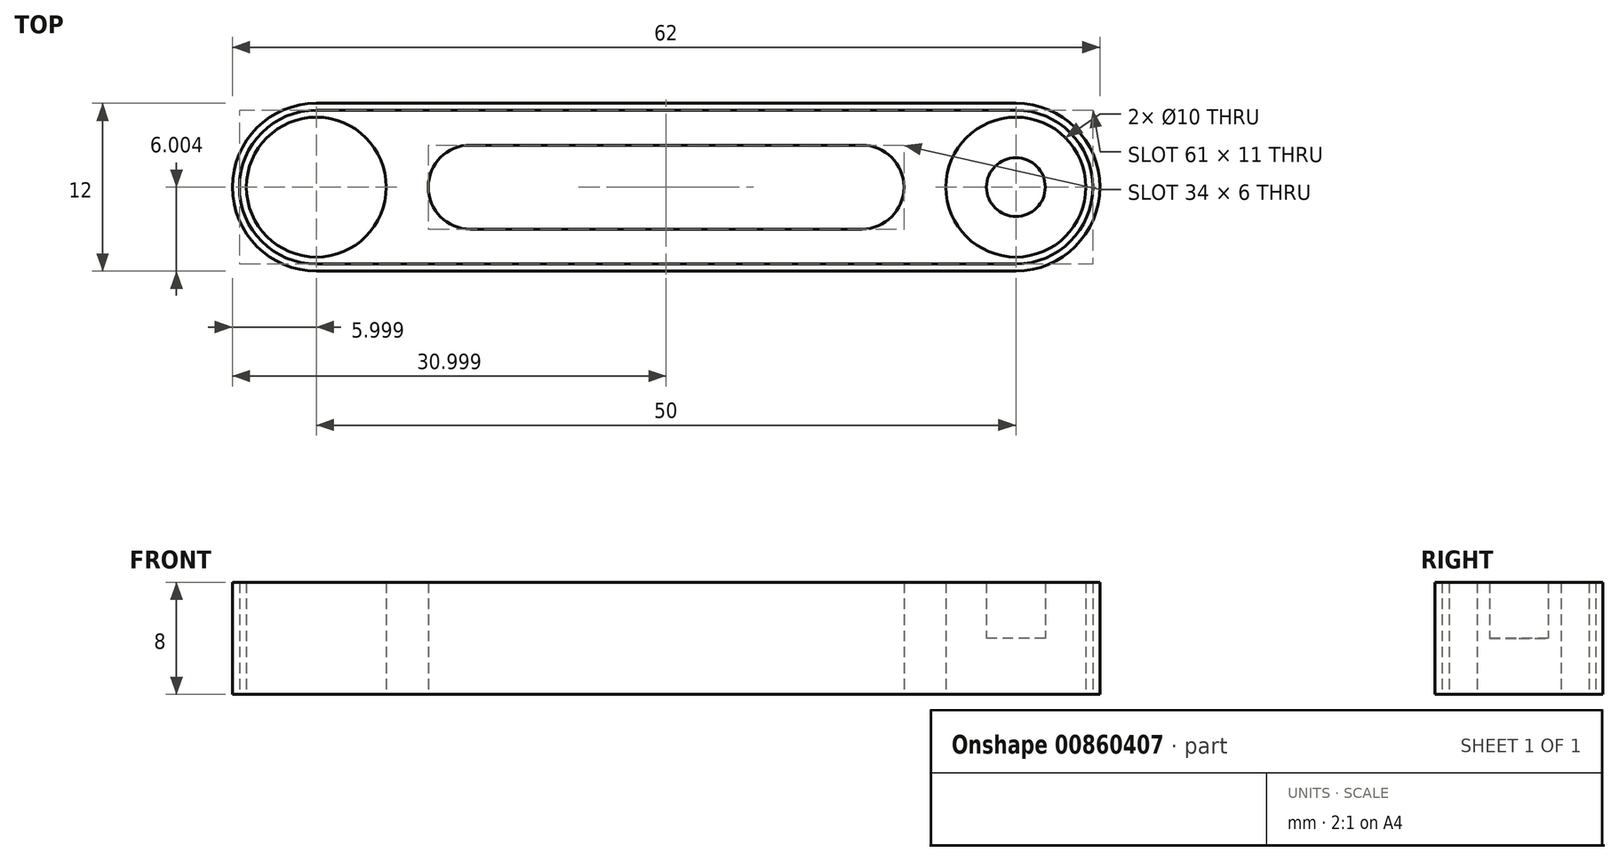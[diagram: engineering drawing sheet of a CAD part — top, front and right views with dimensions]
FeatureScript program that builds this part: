
annotation { "Feature Type Name" : "Feature", "Feature Type Description" : "" }
export const myFeature = defineFeature(function(context is Context, id is Id, definition is map)
    precondition{}
    {
        {
            var Q0;
            Q0=qCreatedBy(makeId("Top.planeOp"),FACE);
            var sketch = newSketch(context, id + "F0", { "sketchPlane" : qUnion([Q0])});
            skLineSegment(sketch, "E0", {"start": v(-96.16, -25.4) * mm, "end": v(-46.16, -25.4) * mm});
            skLineSegment(sketch, "E1", {"start": v(-46.16, -13.4) * mm, "end": v(-96.16, -13.4) * mm});
            skCircle(sketch, "E2", {"center": v(-96.16, -19.4) * mm, "radius": 2.1 * mm});
            skCircle(sketch, "E3", {"center": v(-46.16, -19.4) * mm, "radius": 2.1 * mm});
            skLineSegment(sketch, "E4", {"start": v(-9.27, -13.4) * mm, "end": v(-9.27, -25.4) * mm});
            skLineSegment(sketch, "E5", {"start": v(-1.27, -24.9) * mm, "end": v(-1.27, -13.9) * mm});
            skLineSegment(sketch, "E6", {"start": v(-1.77, -13.4) * mm, "end": v(-9.27, -13.4) * mm});
            skLineSegment(sketch, "E7", {"start": v(-9.27, -17.3) * mm, "end": v(-5.27, -17.3) * mm});
            skLineSegment(sketch, "E8", {"start": v(-9.27, -21.5) * mm, "end": v(-5.27, -21.5) * mm});
            skLineSegment(sketch, "E9", {"start": v(-5.27, -15.4) * mm, "end": v(-1.27, -15.4) * mm});
            skLineSegment(sketch, "E10", {"start": v(-5.27, -23.4) * mm, "end": v(-1.27, -23.4) * mm});
            skCircle(sketch, "E11", {"center": v(-96.16, -19.4) * mm, "radius": 4 * mm});
            skCircle(sketch, "E12", {"center": v(-46.16, -19.4) * mm, "radius": 4 * mm});
            skLineSegment(sketch, "E13", {"start": v(-5.27, -15.4) * mm, "end": v(-5.27, -23.4) * mm});
            skLineSegment(sketch, "E14", {"start": v(-85.16, -16.4) * mm, "end": v(-57.16, -16.4) * mm});
            skLineSegment(sketch, "E15", {"start": v(-57.16, -22.4) * mm, "end": v(-85.16, -22.4) * mm});
            skArc(sketch, "E16", {"start": v(-57.16, -22.4) * mm, "mid": v(-54.16, -19.4) * mm, "end": v(-57.16, -16.4) * mm});
            skArc(sketch, "E17", {"start": v(-85.16, -16.4) * mm, "mid": v(-88.16, -19.4) * mm, "end": v(-85.16, -22.4) * mm});
            skLineSegment(sketch, "E18", {"start": v(-9.27, -16.4) * mm, "end": v(-3.27, -16.4) * mm});
            skLineSegment(sketch, "E19", {"start": v(-3.27, -16.4) * mm, "end": v(-3.27, -22.4) * mm});
            skLineSegment(sketch, "E20", {"start": v(-9.27, -22.4) * mm, "end": v(-3.27, -22.4) * mm});
            skArc(sketch, "E21", {"start": v(-96.16, -13.4) * mm, "mid": v(-102.16, -19.4) * mm, "end": v(-96.16, -25.4) * mm});
            skArc(sketch, "E22", {"start": v(-46.16, -25.4) * mm, "mid": v(-40.16, -19.4) * mm, "end": v(-46.16, -13.4) * mm});
            skLineSegment(sketch, "E23", {"start": v(-46.16, -13.9) * mm, "end": v(-96.16, -13.9) * mm});
            skLineSegment(sketch, "E24", {"start": v(-96.16, -24.9) * mm, "end": v(-46.16, -24.9) * mm});
            skArc(sketch, "E25", {"start": v(-46.16, -24.9) * mm, "mid": v(-40.66, -19.4) * mm, "end": v(-46.16, -13.9) * mm});
            skArc(sketch, "E26", {"start": v(-96.16, -13.9) * mm, "mid": v(-101.66, -19.4) * mm, "end": v(-96.16, -24.9) * mm});
            skLineSegment(sketch, "E27", {"start": v(-9.27, -25.4) * mm, "end": v(-1.77, -25.4) * mm});
            skLineSegment(sketch, "E28", {"start": v(-1.77, -25.4) * mm, "end": v(-1.27, -24.9) * mm});
            skLineSegment(sketch, "E29", {"start": v(-1.77, -13.4) * mm, "end": v(-1.27, -13.9) * mm});
            skLineSegment(sketch, "E30", {"start": v(-1.77, -13.4) * mm, "end": v(-1.77, -25.4) * mm});
            skCircle(sketch, "E31", {"center": v(-46.16, -19.4) * mm, "radius": 5 * mm});
            skCircle(sketch, "E32", {"center": v(-96.16, -19.4) * mm, "radius": 5 * mm});
            skLineSegment(sketch, "E33", {"start": v(-8.27, -14.4) * mm, "end": v(-8.27, -24.4) * mm});
            skLineSegment(sketch, "E34", {"start": v(-46.16, -19.4) * mm, "end": v(-46.16, -28.1) * mm});
            skLineSegment(sketch, "E35", {"start": v(-8.27, -14.4) * mm, "end": v(-9.27, -14.4) * mm});
            skLineSegment(sketch, "E36", {"start": v(-8.27, -24.4) * mm, "end": v(-9.27, -24.4) * mm});
            skSolve(sketch);
        }
        {
            var Q0;
            Q0=makeQuery(id+"F0.imprint","IMPRINT",FACE,{"disambiguationData":[TD([[makeQuery(id+"F0.imprint","IMPRINT",EDGE,{"derivedFrom":sQuery(id+"F0.wireOp",EDGE,"E14")}),1.0]])]});
            extrude(context, id + "F1", {"entities" : qUnion([Q0]), "depth" : 8 * mm, "offsetDistance" : 25 * mm});
        }
        {
            var Q0;
            Q0=makeQuery(id+"F0.imprint","IMPRINT",FACE,{"disambiguationData":[TD([[makeQuery(id+"F0.imprint","IMPRINT",EDGE,{"derivedFrom":sQuery(id+"F0.wireOp",EDGE,"E0")}),1.0]])]});
            var Q1;
            Q1=sQuery(id+"F0.wireOp",EDGE,"E21");
            var Q2;
            Q2=sQuery(id+"F0.wireOp",EDGE,"E26");
            var Q3;
            Q3=sQuery(id+"F0.wireOp",EDGE,"E24");
            var Q4;
            Q4=sQuery(id+"F0.wireOp",EDGE,"E0");
            var Q5;
            Q5=sQuery(id+"F0.wireOp",EDGE,"E22");
            var Q6;
            Q6=sQuery(id+"F0.wireOp",EDGE,"E25");
            var Q7;
            Q7=sQuery(id+"F0.wireOp",EDGE,"E1");
            var Q8;
            Q8=sQuery(id+"F0.wireOp",EDGE,"E23");
            extrude(context, id + "F2", {"entities" : qUnion([Q0]), "surfaceEntities" : qUnion([Q1, Q2, Q3, Q4, Q5, Q6, Q7, Q8]), "depth" : 8 * mm, "offsetDistance" : 25 * mm});
        }
        {
            var Q0;
            Q0=makeQuery(id+"F0.imprint","IMPRINT",FACE,{"disambiguationData":[TD([[makeQuery(id+"F0.imprint","IMPRINT",EDGE,{"derivedFrom":sQuery(id+"F0.wireOp",EDGE,"E3")}),1.0]])]});
            var Q1;
            Q1=makeQuery(id+"F0.imprint","IMPRINT",FACE,{"disambiguationData":[TD([[makeQuery(id+"F0.imprint","IMPRINT",EDGE,{"derivedFrom":sQuery(id+"F0.wireOp",EDGE,"E3")}),-1.0]])]});
            var Q2;
            Q2=makeQuery(id+"F0.imprint","IMPRINT",FACE,{"disambiguationData":[TD([[makeQuery(id+"F0.imprint","IMPRINT",EDGE,{"derivedFrom":sQuery(id+"F0.wireOp",EDGE,"E12")}),1.0]])]});
            extrude(context, id + "F3", {"entities" : qUnion([Q0, Q1, Q2]), "operationType" : NewBodyOperationType.ADD, "depth" : 8 * mm, "offsetDistance" : 25 * mm});
        }
        {
            var Q0;
            Q0=makeQuery(id+"F0.imprint","IMPRINT",FACE,{"disambiguationData":[TD([[makeQuery(id+"F0.imprint","IMPRINT",EDGE,{"derivedFrom":sQuery(id+"F0.wireOp",EDGE,"E12")}),1.0]])]});
            extrude(context, id + "F4", {"entities" : qUnion([Q0]), "operationType" : NewBodyOperationType.REMOVE, "depth" : 1 * mm, "offsetDistance" : 25 * mm});
        }
        {
            var Q0;
            Q0=makeQuery(id+"F0.imprint","IMPRINT",FACE,{"disambiguationData":[TD([[makeQuery(id+"F0.imprint","IMPRINT",EDGE,{"derivedFrom":sQuery(id+"F0.wireOp",EDGE,"E3")}),-1.0]])]});
            extrude(context, id + "F5", {"entities" : qUnion([Q0]), "operationType" : NewBodyOperationType.REMOVE, "depth" : 8 * mm, "offsetDistance" : 25 * mm});
        }
        {
            var Q0;
            Q0=makeQuery(id+"F0.imprint","IMPRINT",FACE,{"disambiguationData":[TD([[makeQuery(id+"F0.imprint","IMPRINT",EDGE,{"derivedFrom":sQuery(id+"F0.wireOp",EDGE,"E3")}),1.0]])]});
            extrude(context, id + "F6", {"entities" : qUnion([Q0]), "operationType" : NewBodyOperationType.REMOVE, "depth" : 4 * mm, "offsetDistance" : 25 * mm});
        }
    });
